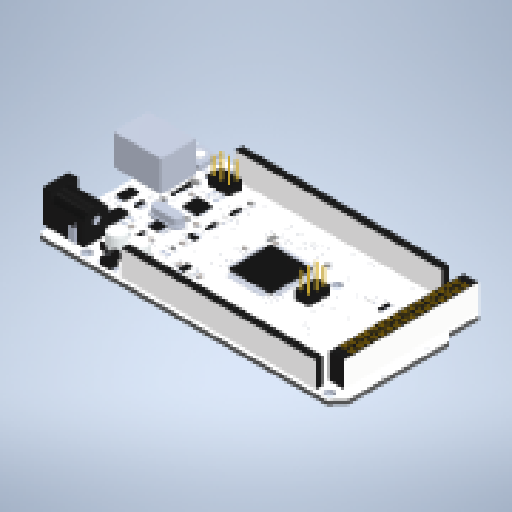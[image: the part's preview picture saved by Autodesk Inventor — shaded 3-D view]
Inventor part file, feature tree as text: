
AUTODESK INVENTOR PART (.ipt)
format: ipt  version: 2023.1 (Build 271208000, 208)  size: 4,282,368 bytes
history: native  units: in
note: dims shown in document units (in); Inventor stores cm internally (conversion verified against a paired STEP export)
features: other x1, fillet x1
ambient origin geometry x8: Origin, YZ Plane, XZ Plane, XY Plane, X Axis, Y Axis, Z Axis, Center Point
bodies: Solid1 (feature_tree)
feature tree (2):
  other  "Work Point7"
  fillet  "Fillet13"  [1 undecoded]
note: 1 required parameter value undecoded (feature->parameter linkage not recoverable at this tier; creation-order binding heuristic only, values carry confidence <= 0.55)
